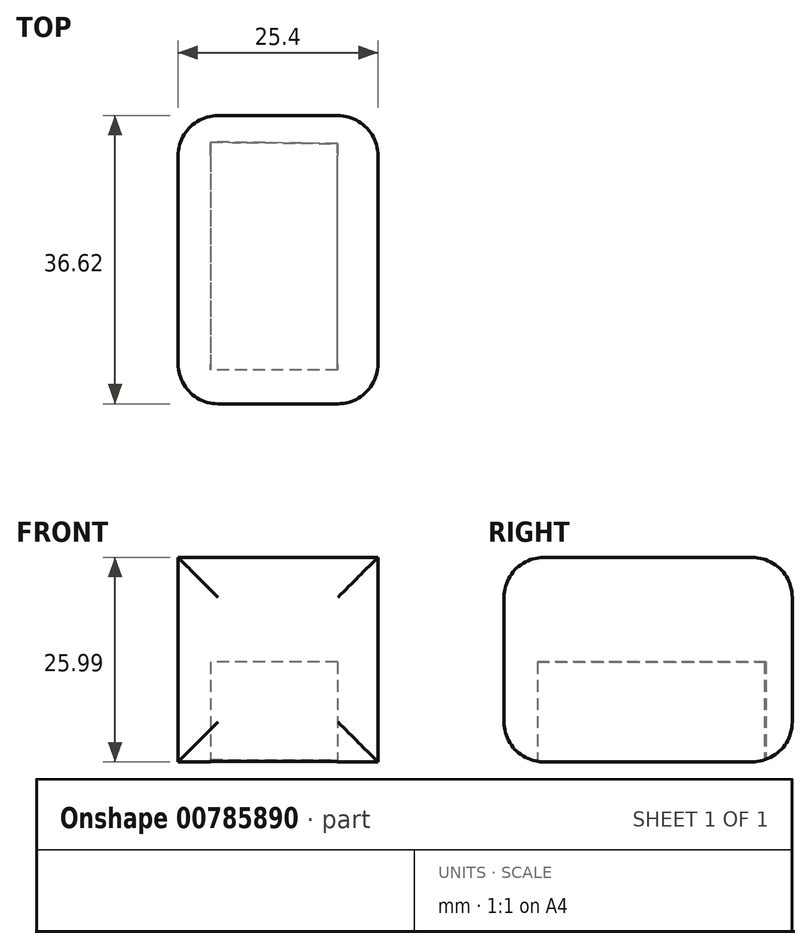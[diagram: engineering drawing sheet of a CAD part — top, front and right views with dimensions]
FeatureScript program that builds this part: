
annotation { "Feature Type Name" : "Feature", "Feature Type Description" : "" }
export const myFeature = defineFeature(function(context is Context, id is Id, definition is map)
    precondition{}
    {
        {
            var Q0;
            Q0=qCreatedBy(makeId("Right.planeOp"),FACE);
            var sketch = newSketch(context, id + "F0", { "sketchPlane" : qUnion([Q0])});
            skLineSegment(sketch, "E0.bottom", {"start": v(0, 0) * mm, "end": v(-36.62, 0) * mm});
            skLineSegment(sketch, "E0.top", {"start": v(0, 25.99) * mm, "end": v(-36.62, 25.99) * mm});
            skLineSegment(sketch, "E0.left", {"start": v(0, 0) * mm, "end": v(0, 25.99) * mm});
            skLineSegment(sketch, "E0.right", {"start": v(-36.62, 0) * mm, "end": v(-36.62, 25.99) * mm});
            skSolve(sketch);
        }
        {
            var Q0;
            Q0 = qSketchRegion(id + "F0", true);
            extrude(context, id + "F1", {"entities" : qUnion([Q0]), "depth" : 25.4 * mm, "offsetDistance" : 25.4 * mm});
        }
        {
            var Q0;
            Q0=qCreatedBy(makeId("Top.planeOp"),FACE);
            var sketch = newSketch(context, id + "F2", { "sketchPlane" : qUnion([Q0])});
            skLineSegment(sketch, "E1", {"start": v(4.14, -3.37) * mm, "end": v(4.14, -32.34) * mm});
            skLineSegment(sketch, "E2", {"start": v(4.14, -32.34) * mm, "end": v(20.26, -32.34) * mm});
            skLineSegment(sketch, "E3", {"start": v(20.26, -32.34) * mm, "end": v(20.26, -3.56) * mm});
            skLineSegment(sketch, "E4", {"start": v(20.26, -3.56) * mm, "end": v(4.14, -3.37) * mm});
            skSolve(sketch);
        }
        {
            var Q0;
            Q0=makeQuery(id+"F2.imprint","IMPRINT",FACE,{"disambiguationData":[TD([[makeQuery(id+"F2.imprint","IMPRINT",EDGE,{"derivedFrom":sQuery(id+"F2.wireOp",EDGE,"E1")}),1.0]])]});
            extrude(context, id + "F3", {"entities" : qUnion([Q0]), "operationType" : NewBodyOperationType.ADD, "depth" : 12.7 * mm, "offsetDistance" : 25.4 * mm});
        }
        {
            var Q0;
            Q0 = qSketchRegion(id + "F2", true);
            extrude(context, id + "F4", {"entities" : qUnion([Q0]), "operationType" : NewBodyOperationType.REMOVE, "depth" : 12.7 * mm, "offsetDistance" : 25.4 * mm});
        }
        {
            var Q0;
            Q0=makeQuery(id+"F1.opExtrude","SWEPT_FACE",FACE,{"disambiguationData":[OSD([sQuery(id+"F0.wireOp",EDGE,"E0.right")])]});
            fillet(context, id + "F5", {"entities" : qUnion([Q0]), "radius" : 5.08 * mm, "tangentPropagation" : true, "allowEdgeOverflow" : false});
        }
        {
            var Q0;
            Q0=makeQuery(id+"F1.opExtrude","SWEPT_FACE",FACE,{"disambiguationData":[OSD([sQuery(id+"F0.wireOp",EDGE,"E0.left")])]});
            fillet(context, id + "F6", {"entities" : qUnion([Q0]), "radius" : 5.08 * mm, "tangentPropagation" : true, "allowEdgeOverflow" : false});
        }
    });
